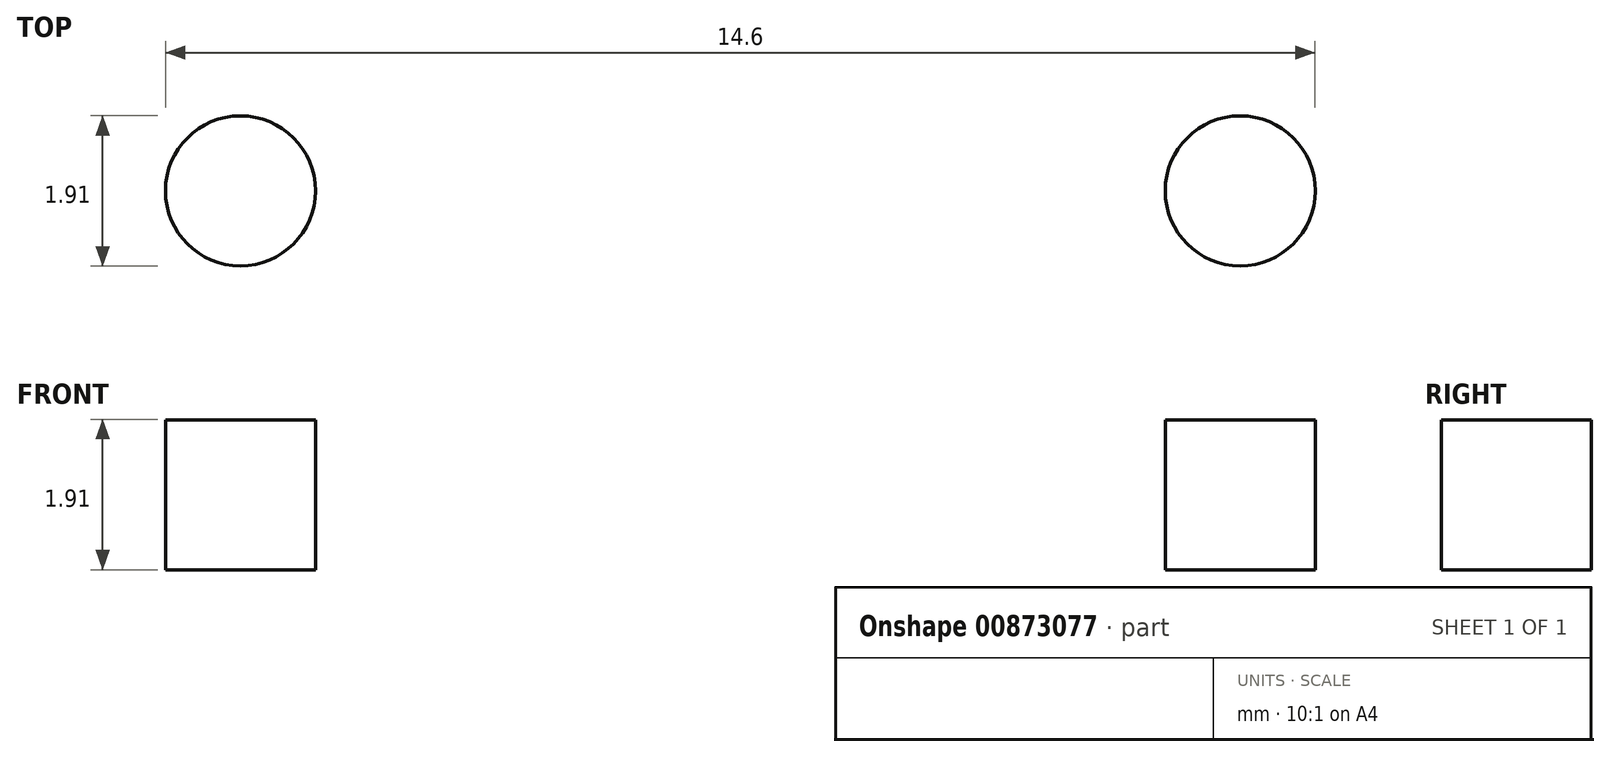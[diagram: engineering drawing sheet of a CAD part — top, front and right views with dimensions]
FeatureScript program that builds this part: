
annotation { "Feature Type Name" : "Feature", "Feature Type Description" : "" }
export const myFeature = defineFeature(function(context is Context, id is Id, definition is map)
    precondition{}
    {
        {
            var Q0;
            Q0=qCreatedBy(makeId("Top.planeOp"),FACE);
            var sketch = newSketch(context, id + "F0", { "sketchPlane" : qUnion([Q0])});
            skLineSegment(sketch, "E0.bottom", {"start": v(10.8, -34.93) * mm, "end": v(-10.8, -34.93) * mm});
            skLineSegment(sketch, "E0.top", {"start": v(10.8, 34.93) * mm, "end": v(-10.8, 34.93) * mm});
            skLineSegment(sketch, "E0.left", {"start": v(-10.8, 34.93) * mm, "end": v(-10.8, -34.93) * mm});
            skLineSegment(sketch, "E0.right", {"start": v(10.8, 34.93) * mm, "end": v(10.8, -34.93) * mm});
            skLineSegment(sketch, "E1.bottom", {"start": v(5.33, 25.4) * mm, "end": v(2.16, 25.4) * mm});
            skLineSegment(sketch, "E1.top", {"start": v(5.33, -25.4) * mm, "end": v(2.16, -25.4) * mm});
            skLineSegment(sketch, "E1.left", {"start": v(5.33, 25.4) * mm, "end": v(5.33, -25.4) * mm});
            skLineSegment(sketch, "E1.right", {"start": v(-5.33, 25.4) * mm, "end": v(-5.33, -25.4) * mm});
            skPoint(sketch, "E1.middle", {"position": v(0, 0) * mm});
            skLineSegment(sketch, "E2", {"start": v(10.8, 34.93) * mm, "end": v(-10.8, -34.93) * mm, "construction": true});
            skLineSegment(sketch, "E3", {"start": v(0, 34.93) * mm, "end": v(0, -34.92) * mm, "construction": true});
            skPoint(sketch, "E4", {"position": v(0, 25.4) * mm});
            skLineSegment(sketch, "E5.bottom", {"start": v(2.16, 25.15) * mm, "end": v(-2.16, 25.15) * mm});
            skLineSegment(sketch, "E5.left", {"start": v(2.16, 25.15) * mm, "end": v(2.16, 25.4) * mm});
            skLineSegment(sketch, "E5.right", {"start": v(-2.16, 25.15) * mm, "end": v(-2.16, 25.4) * mm});
            skPoint(sketch, "E5.middle", {"position": v(0, 25.27) * mm});
            skLineSegment(sketch, "E6", {"start": v(-10.8, 0) * mm, "end": v(10.8, 0) * mm, "construction": true});
            skLineSegment(sketch, "E7.MirrorCS", {"start": v(2.16, -25.15) * mm, "end": v(2.16, -25.4) * mm});
            skLineSegment(sketch, "E8.MirrorCS", {"start": v(2.16, -25.15) * mm, "end": v(-2.16, -25.15) * mm});
            skLineSegment(sketch, "E9.MirrorCS", {"start": v(-2.16, -25.15) * mm, "end": v(-2.16, -25.4) * mm});
            skLineSegment(sketch, "E10.trimOffspring", {"start": v(-2.16, -25.4) * mm, "end": v(-5.33, -25.4) * mm});
            skLineSegment(sketch, "E11.trimOffspring", {"start": v(-2.16, 25.4) * mm, "end": v(-5.33, 25.4) * mm});
            skSolve(sketch);
        }
        {
            var Q0;
            Q0 = qSketchRegion(id + "F0", true);
            extrude(context, id + "F1", {"entities" : qUnion([Q0]), "depth" : 1.9 * mm, "offsetDistance" : 25.4 * mm});
        }
        {
            var Q0;
            Q0=qCreatedBy(makeId("Top.planeOp"),FACE);
            var sketch = newSketch(context, id + "F2", { "sketchPlane" : qUnion([Q0])});
            skLineSegment(sketch, "E12.bottom", {"start": v(-2.16, -25.4) * mm, "end": v(-5.33, -25.4) * mm});
            skLineSegment(sketch, "E12.top", {"start": v(-2.16, 25.4) * mm, "end": v(-5.33, 25.4) * mm});
            skLineSegment(sketch, "E12.left", {"start": v(-2.16, -25.4) * mm, "end": v(-2.16, 25.4) * mm});
            skLineSegment(sketch, "E12.right", {"start": v(-5.33, -25.4) * mm, "end": v(-5.33, 25.4) * mm});
            skLineSegment(sketch, "E13", {"start": v(0, 25.05) * mm, "end": v(0, -25.13) * mm, "construction": true});
            skLineSegment(sketch, "E14.MirrorCS", {"start": v(2.16, 25.4) * mm, "end": v(5.33, 25.4) * mm});
            skLineSegment(sketch, "E15.MirrorCS", {"start": v(2.16, -25.4) * mm, "end": v(2.16, 25.4) * mm});
            skLineSegment(sketch, "E16.MirrorCS", {"start": v(5.33, -25.4) * mm, "end": v(5.33, 25.4) * mm});
            skLineSegment(sketch, "E17.MirrorCS", {"start": v(2.16, -25.4) * mm, "end": v(5.33, -25.4) * mm});
            skSolve(sketch);
        }
        {
            var Q0;
            Q0=makeQuery(id+"F1.opExtrude","CAP_FACE",FACE,{"disambiguationData":[OSD([sQuery(id+"F0.wireOp",EDGE,"E0.bottom"),sQuery(id+"F0.wireOp",EDGE,"E0.top"),sQuery(id+"F0.wireOp",EDGE,"E0.left"),sQuery(id+"F0.wireOp",EDGE,"E0.right"),sQuery(id+"F0.wireOp",EDGE,"E1.bottom"),sQuery(id+"F0.wireOp",EDGE,"E1.top"),sQuery(id+"F0.wireOp",EDGE,"E1.left"),sQuery(id+"F0.wireOp",EDGE,"E1.right"),sQuery(id+"F0.wireOp",EDGE,"E5.bottom"),sQuery(id+"F0.wireOp",EDGE,"E5.left"),sQuery(id+"F0.wireOp",EDGE,"E5.right"),sQuery(id+"F0.wireOp",EDGE,"E7.MirrorCS"),sQuery(id+"F0.wireOp",EDGE,"E8.MirrorCS"),sQuery(id+"F0.wireOp",EDGE,"E9.MirrorCS"),sQuery(id+"F0.wireOp",EDGE,"E10.trimOffspring"),sQuery(id+"F0.wireOp",EDGE,"E11.trimOffspring")])],"isStart":true});
            var sketch = newSketch(context, id + "F3", { "sketchPlane" : qUnion([Q0])});
            skLineSegment(sketch, "E18", {"start": v(0, -25.15) * mm, "end": v(0, -34.93) * mm, "construction": true});
            skLineSegment(sketch, "E19", {"start": v(-10.8, -30.04) * mm, "end": v(10.8, -30.04) * mm, "construction": true});
            skPoint(sketch, "E19.startSnap0", {"position": v(0, -30.04) * mm});
            skCircle(sketch, "E20", {"center": v(-6.35, -30.04) * mm, "radius": 0.95 * mm});
            skCircle(sketch, "E21", {"center": v(6.35, -30.04) * mm, "radius": 0.95 * mm});
            skCircle(sketch, "E22.MirrorC", {"center": v(6.35, 30.04) * mm, "radius": 0.95 * mm});
            skCircle(sketch, "E23.MirrorC", {"center": v(-6.35, 30.04) * mm, "radius": 0.95 * mm});
            skSolve(sketch);
        }
        {
            var Q0;
            Q0=makeQuery(id+"F3.imprint","IMPRINT",FACE,{"disambiguationData":[TD([[makeQuery(id+"F3.imprint","IMPRINT",EDGE,{"derivedFrom":sQuery(id+"F3.wireOp",EDGE,"E22.MirrorC")}),-1.0]])]});
            var Q1;
            Q1=makeQuery(id+"F3.imprint","IMPRINT",FACE,{"disambiguationData":[TD([[makeQuery(id+"F3.imprint","IMPRINT",EDGE,{"derivedFrom":sQuery(id+"F3.wireOp",EDGE,"E23.MirrorC")}),-1.0]])]});
            var Q2;
            Q2=makeQuery(id+"F3.imprint","IMPRINT",FACE,{"disambiguationData":[TD([[makeQuery(id+"F3.imprint","IMPRINT",EDGE,{"derivedFrom":sQuery(id+"F3.wireOp",EDGE,"E21")}),1.0]])]});
            var Q3;
            Q3=makeQuery(id+"F3.imprint","IMPRINT",FACE,{"disambiguationData":[TD([[makeQuery(id+"F3.imprint","IMPRINT",EDGE,{"derivedFrom":sQuery(id+"F3.wireOp",EDGE,"E20")}),1.0]])]});
            extrude(context, id + "F4", {"entities" : qUnion([Q0, Q1, Q2, Q3]), "operationType" : NewBodyOperationType.REMOVE, "oppositeDirection" : true, "depth" : 25.4 * mm, "offsetDistance" : 25.4 * mm});
        }
    });
